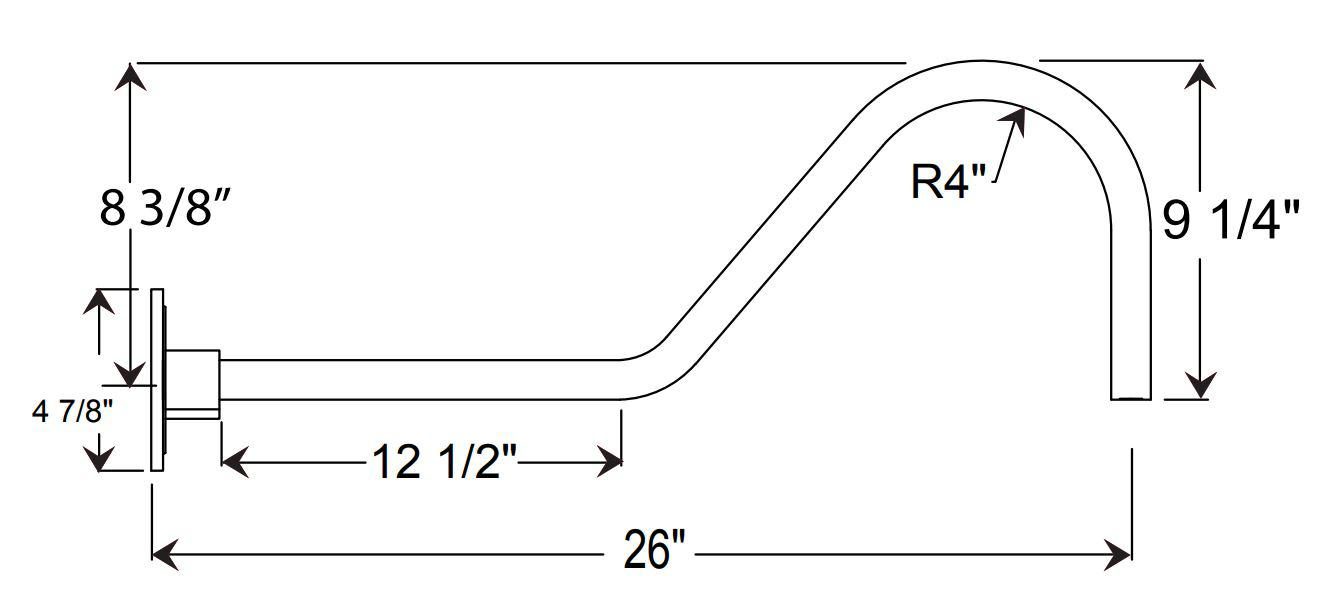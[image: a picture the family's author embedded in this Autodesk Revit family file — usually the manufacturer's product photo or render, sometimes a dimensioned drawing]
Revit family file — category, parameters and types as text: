
# Revit family: OSGG(24,30,36) MB
name_source: partatom
category: Lighting Fixtures
units: mm (PartAtom-declared; Revit-internal decimal feet)

## family parameters
Always vertical = Yes
Cut with Voids When Loaded = No
Light Source = Yes
OmniClass Number = 23.80.70.00
OmniClass Title = Lighting
Part Type = Normal
Room Calculation Point = No
Round Connector Dimension = Use Diameter
Shared = No
Work Plane-Based = No

## types (3) — shared parameters
Apparent Load = 200 VA
Body Colour = Spun aluminium
Body Material = body
Bulb = Bulb
CRI = >90
Color Filter = 16777215
Construction Material = Heavy Duty spun aluminum.
Default Elevation = 0' - 0"
Description = 120-277 Voltage
Dimming = 1%
Dimming Lamp Color Temperature Shift = <None>
Efficiency = 65-125 lumens per watt
Inside body material = INSIDE BODY
Lamp = MB
Life = L70 50,000 hours
Load Classification = Lighting
Manufacturer = ANP Lighting
Photometric Web File = OSGG36M037LDDW35K.ies
Power Factor = 1
Tilt Angle = 90.00°
URL = https://www.anplighting.com
Voltage = 277 V
Warranty = 5 year limited warranty
Wattage Comments = 200W Max

## per-type parameters (varying)
| type | Fixture Diameter | Fixture Height | OSGG24 | OSGG30 | OSGG36 | Weight |
| OSGG 24 | 2' - 0" | 2' - 2" | Yes | No | No | 19 lb |
| OSGG 30 | 2' - 6" | 1' - 7" | No | Yes | No | 15 lb |
| OSGG 36 | 3' - 0" | 3' - 4" | No | No | Yes | 41 lb |

note: column(s) folded — value = type name in every type: Model

## geometry (parser evidence)
native form markers: Sweep x39
no freeform markers — native parametric forms only
